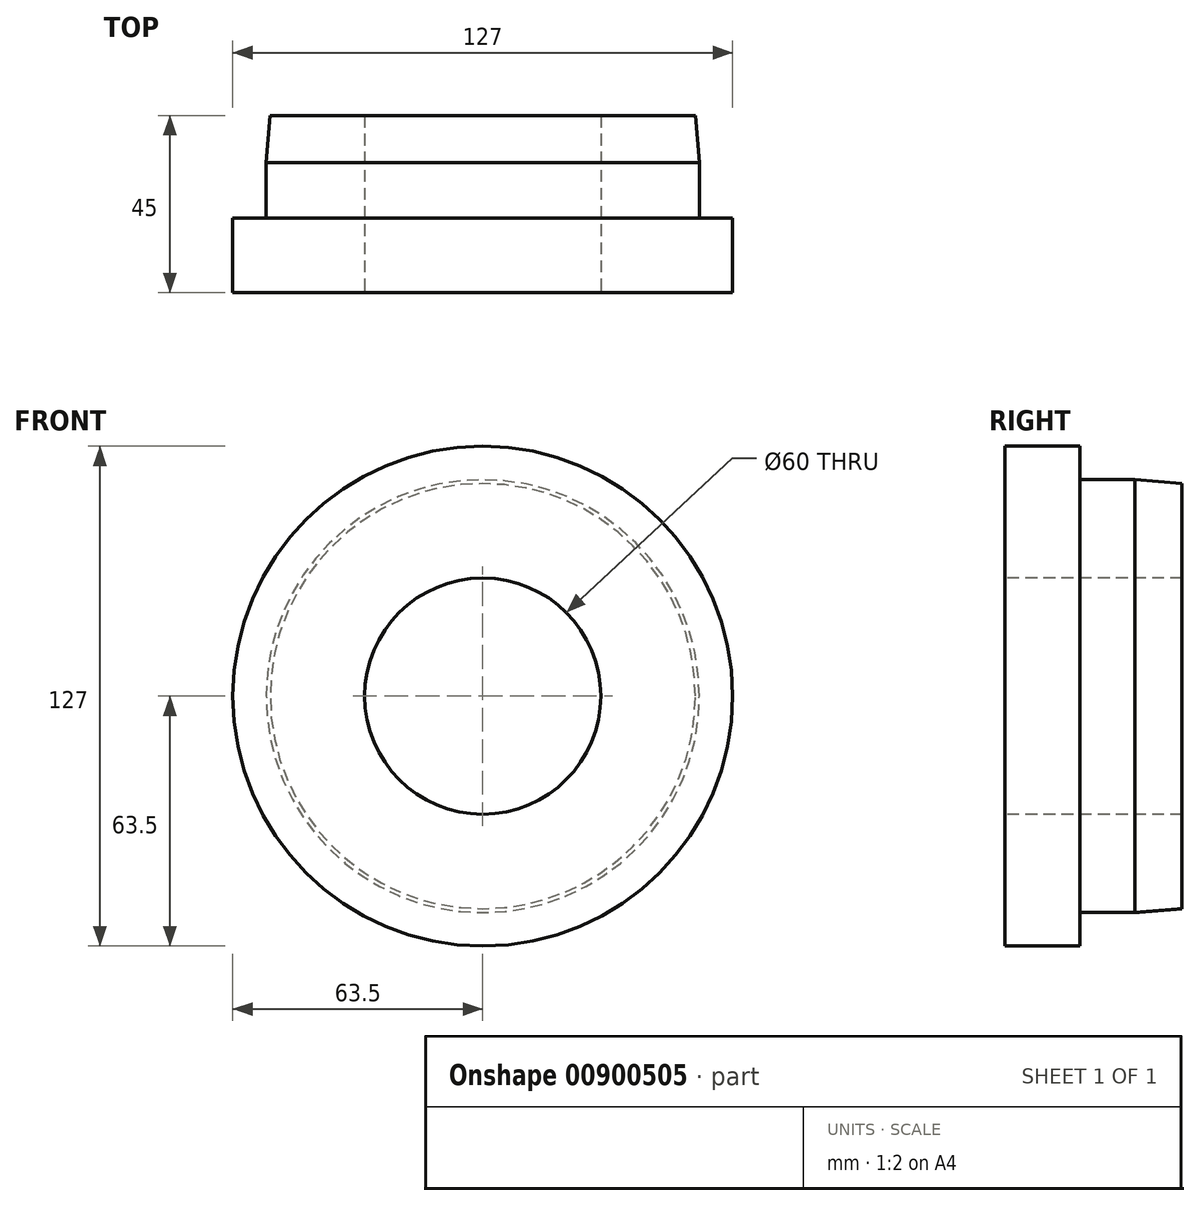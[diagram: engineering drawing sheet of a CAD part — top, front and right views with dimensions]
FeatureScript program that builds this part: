
annotation { "Feature Type Name" : "Feature", "Feature Type Description" : "" }
export const myFeature = defineFeature(function(context is Context, id is Id, definition is map)
    precondition{}
    {
        {
            var Q0;
            Q0=qCreatedBy(makeId("Right.planeOp"),FACE);
            var sketch = newSketch(context, id + "F0", { "sketchPlane" : qUnion([Q0])});
            skLineSegment(sketch, "E0", {"start": v(0, 30) * mm, "end": v(0, 63.5) * mm});
            skLineSegment(sketch, "E1", {"start": v(0, 63.5) * mm, "end": v(19, 63.5) * mm});
            skLineSegment(sketch, "E2", {"start": v(19, 63.5) * mm, "end": v(19, 55) * mm});
            skLineSegment(sketch, "E3", {"start": v(19, 55) * mm, "end": v(33, 55) * mm});
            skLineSegment(sketch, "E4", {"start": v(33, 55) * mm, "end": v(45, 54) * mm});
            skLineSegment(sketch, "E5", {"start": v(45, 54) * mm, "end": v(45, 30) * mm});
            skLineSegment(sketch, "E6", {"start": v(45, 30) * mm, "end": v(0, 30) * mm});
            skLineSegment(sketch, "E7", {"start": v(-64.86, 0) * mm, "end": v(94.5, 0) * mm, "construction": true});
            skSolve(sketch);
        }
        {
            var Q0;
            Q0=makeQuery(id+"F0.imprint","IMPRINT",FACE,{"disambiguationData":[TD([[makeQuery(id+"F0.imprint","IMPRINT",EDGE,{"derivedFrom":sQuery(id+"F0.wireOp",EDGE,"E0")}),-1.0]])]});
            var Q1;
            Q1=sQuery(id+"F0.wireOp",EDGE,"E7");
            revolve(context, id + "F1", {"surfaceOperationType" : NewSurfaceOperationType.NEW, "entities" : qUnion([Q0]), "axis" : qUnion([Q1]), "revolveType" : RevolveType.FULL});
        }
    });
